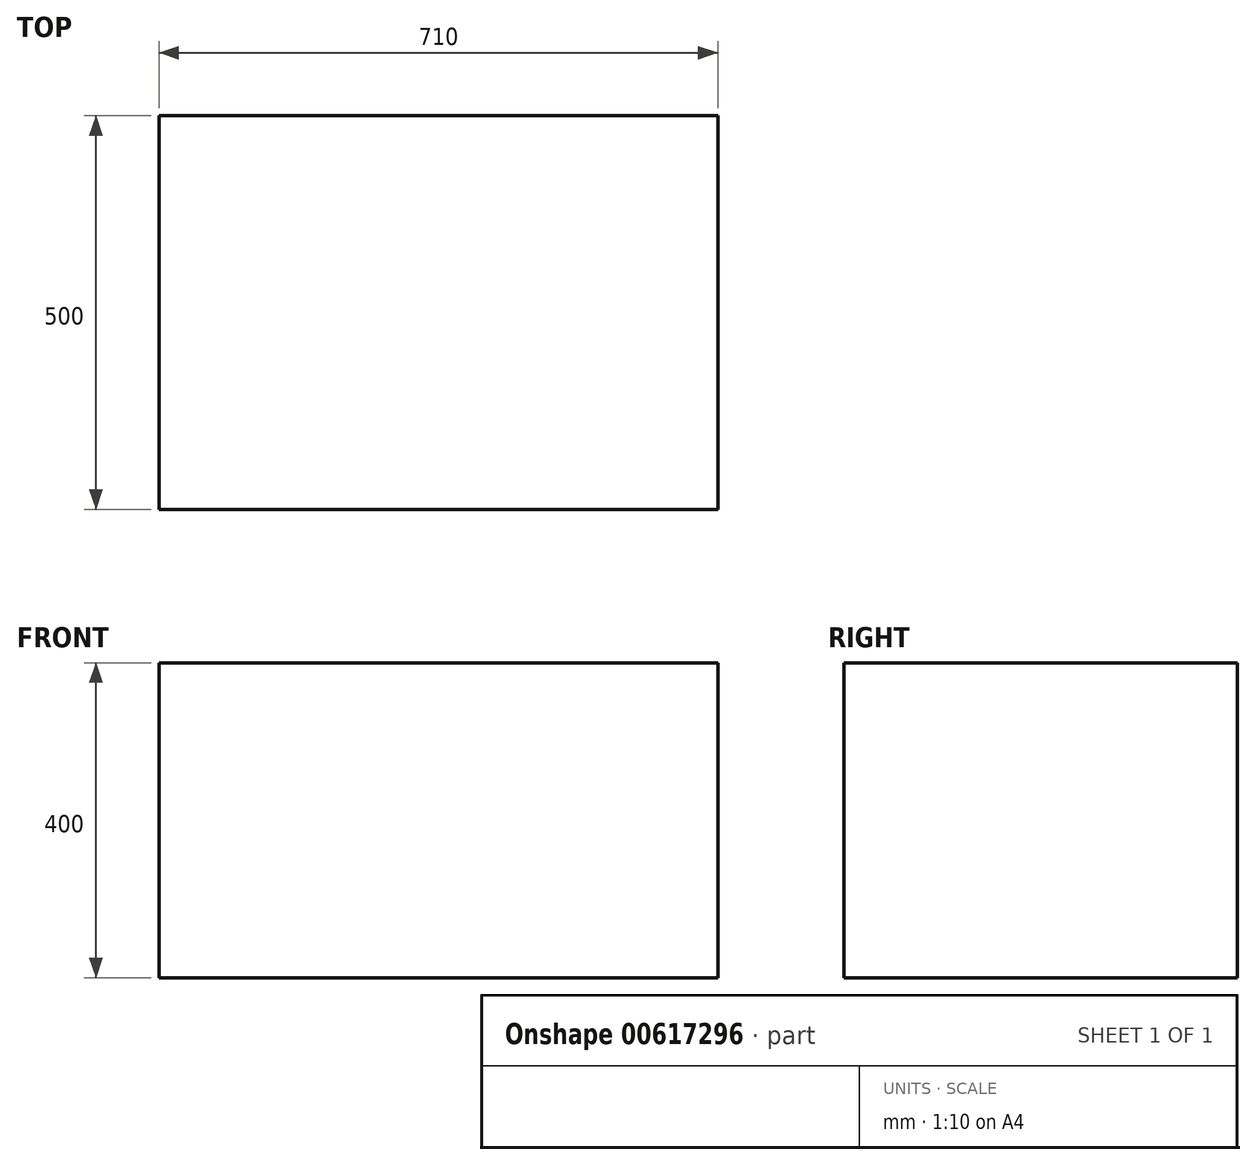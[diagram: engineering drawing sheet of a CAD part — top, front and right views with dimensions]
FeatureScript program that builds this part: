
annotation { "Feature Type Name" : "Feature", "Feature Type Description" : "" }
export const myFeature = defineFeature(function(context is Context, id is Id, definition is map)
    precondition{}
    {
        {
            var Q0;
            Q0=qCreatedBy(makeId("Top.planeOp"),FACE);
            var sketch = newSketch(context, id + "F0", { "sketchPlane" : qUnion([Q0])});
            skLineSegment(sketch, "E0.bottom", {"start": v(-333.12, 363.17) * mm, "end": v(376.88, 363.17) * mm});
            skLineSegment(sketch, "E0.top", {"start": v(-333.12, -136.83) * mm, "end": v(376.88, -136.83) * mm});
            skLineSegment(sketch, "E0.left", {"start": v(-333.12, 363.17) * mm, "end": v(-333.12, -136.83) * mm});
            skLineSegment(sketch, "E0.right", {"start": v(376.88, 363.17) * mm, "end": v(376.88, -136.83) * mm});
            skSolve(sketch);
        }
        {
            var Q0;
            Q0=makeQuery(id+"F0.imprint","IMPRINT",FACE,{"disambiguationData":[TD([[makeQuery(id+"F0.imprint","IMPRINT",EDGE,{"derivedFrom":sQuery(id+"F0.wireOp",EDGE,"E0.bottom")}),-1.0]])]});
            extrude(context, id + "F1", {"entities" : qUnion([Q0]), "depth" : 400 * mm, "offsetDistance" : 25 * mm});
        }
    });
